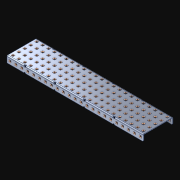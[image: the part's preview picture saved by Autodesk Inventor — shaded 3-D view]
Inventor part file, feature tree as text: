
AUTODESK INVENTOR PART (.ipt)
format: ipt  version: 2021 (Build 250183000, 183)  size: 2,080,256 bytes
history: native  units: in
note: dims shown in document units (in); Inventor stores cm internally (conversion verified against a paired STEP export)
features: extrude x162, other x162, sketch x4, pattern_linear x3
ambient origin geometry x8: Origin, YZ Plane, XZ Plane, XY Plane, X Axis, Y Axis, Z Axis, Center Point
bodies: Solid1 (feature_tree)
feature tree (331):
  pattern_linear  "Rectangular Pattern1"  Spacing1=0.182in  [1 undecoded]
  pattern_linear  "Rectangular Pattern2"  Spacing1=0.046in  [1 undecoded]
  pattern_linear  "Rectangular Pattern3"  Spacing1=0.5in  [1 undecoded]
  extrude  "Extrusion1"  Depth=0.046in
  sketch  "Sketch1"  dims[d0=0.182in]
  other  "Srf1"
  sketch  "Sketch2"  dims[d1=0.046in d2=0.0in]
  other  "Srf2"
  sketch  "Sketch3"  dims[d3=0.182in]
  other  "Srf3"
  other  "Srf4"
  other  "Srf5"
  other  "Srf6"
  other  "Srf7"
  other  "Srf8"
  other  "Srf9"
  other  "Srf10"
  other  "Srf11"
  other  "Srf12"
  other  "Srf13"
  other  "Srf14"
  other  "Srf15"
  other  "Srf16"
  other  "Srf17"
  other  "Srf18"
  other  "Srf19"
  other  "Srf20"
  other  "Srf21"
  other  "Srf22"
  other  "Srf23"
  other  "Srf24"
  other  "Srf25"
  other  "Srf38"
  other  "Srf39"
  other  "Srf40"
  other  "Srf41"
  other  "Srf42"
  other  "Srf43"
  other  "Srf44"
  other  "Srf45"
  other  "Srf46"
  other  "Srf47"
  other  "Srf48"
  other  "Srf49"
  other  "Srf50"
  other  "Srf51"
  other  "Srf52"
  other  "Srf53"
  other  "Srf54"
  other  "Srf55"
  other  "Srf56"
  other  "Srf57"
  other  "Srf58"
  other  "Srf59"
  other  "Srf72"
  other  "Srf73"
  other  "Srf74"
  other  "Srf75"
  other  "Srf76"
  other  "Srf77"
  other  "Srf78"
  other  "Srf79"
  other  "Srf80"
  other  "Srf81"
  other  "Srf82"
  other  "Srf83"
  other  "Srf84"
  other  "Srf85"
  other  "Srf86"
  other  "Srf87"
  other  "Srf88"
  other  "Srf89"
  other  "Srf90"
  other  "Srf91"
  other  "Srf92"
  other  "Srf93"
  other  "Srf94"
  other  "Srf107"
  other  "Srf108"
  other  "Srf109"
  other  "Srf110"
  other  "Srf111"
  other  "Srf112"
  other  "Srf113"
  other  "Srf114"
  other  "Srf115"
  other  "Srf116"
  other  "Srf117"
  other  "Srf118"
  other  "Srf119"
  other  "Srf120"
  other  "Srf121"
  other  "Srf122"
  other  "Srf123"
  other  "Srf124"
  other  "Srf125"
  other  "Srf126"
  other  "Srf127"
  other  "Srf128"
  other  "Srf129"
  other  "Srf142"
  other  "Srf143"
  other  "Srf144"
  other  "Srf145"
  other  "Srf146"
  other  "Srf147"
  other  "Srf148"
  other  "Srf149"
  other  "Srf150"
  other  "Srf151"
  other  "Srf152"
  other  "Srf153"
  other  "Srf154"
  other  "Srf155"
  other  "Srf156"
  other  "Srf157"
  other  "Srf158"
  other  "Srf159"
  other  "Srf160"
  other  "Srf161"
  other  "Srf162"
  other  "Srf163"
  other  "Srf164"
  other  "Srf177"
  other  "Srf178"
  other  "Srf179"
  other  "Srf180"
  other  "Srf181"
  other  "Srf182"
  other  "Srf183"
  other  "Srf184"
  other  "Srf185"
  other  "Srf186"
  other  "Srf187"
  other  "Srf188"
  other  "Srf189"
  other  "Srf190"
  other  "Srf191"
  other  "Srf192"
  other  "Srf193"
  other  "Srf194"
  other  "Srf195"
  other  "Srf196"
  other  "Srf197"
  other  "Srf198"
  other  "Srf199"
  other  "Srf212"
  other  "Srf213"
  other  "Srf214"
  other  "Srf215"
  other  "Srf216"
  other  "Srf217"
  other  "Srf218"
  other  "Srf219"
  other  "Srf220"
  other  "Srf221"
  other  "Srf222"
  other  "Srf223"
  other  "Srf224"
  other  "Srf225"
  other  "Srf226"
  other  "Srf227"
  other  "Srf228"
  other  "Srf229"
  other  "Srf230"
  other  "Srf231"
  other  "Srf232"
  other  "Srf233"
  sketch  "Sketch4"  dims[d4=0.046in d5=0.0in d6=0.182in d7=0.046in d8=0.0in d11=0.5in d12=9.0551in d14=0.5in d15=1.9685in d17=0.5in d18=9.0551in d20=0.5in d21=6.0in d22=0.0in]
  parser-record x1  (decoder bookkeeping rows leaked as tree rows — omitted from the tree; the rows remain in map.json)
  extrude  "ExtrusionSrf1"  Depth=0.046in
  extrude  "ExtrusionSrf2"  Depth=0.046in
  extrude  "ExtrusionSrf3"  Depth=0.046in
  extrude  "ExtrusionSrf4"  Depth=0.046in
  extrude  "ExtrusionSrf5"  Depth=0.046in
  extrude  "ExtrusionSrf6"  TaperAngle=0.0deg  [1 undecoded]
  extrude  "ExtrusionSrf7"  [1 undecoded]
  extrude  "ExtrusionSrf8"  [1 undecoded]
  extrude  "ExtrusionSrf9"  [1 undecoded]
  extrude  "ExtrusionSrf10"  [1 undecoded]
  extrude  "ExtrusionSrf11"  [1 undecoded]
  extrude  "ExtrusionSrf12"  [1 undecoded]
  extrude  "ExtrusionSrf13"  [1 undecoded]
  extrude  "ExtrusionSrf14"  [1 undecoded]
  extrude  "ExtrusionSrf15"  [1 undecoded]
  extrude  "ExtrusionSrf16"  [1 undecoded]
  extrude  "ExtrusionSrf17"  [1 undecoded]
  extrude  "ExtrusionSrf18"  [1 undecoded]
  extrude  "ExtrusionSrf19"  [1 undecoded]
  extrude  "ExtrusionSrf20"  [1 undecoded]
  extrude  "ExtrusionSrf21"  [1 undecoded]
  extrude  "ExtrusionSrf22"  [1 undecoded]
  extrude  "ExtrusionSrf23"  [1 undecoded]
  extrude  "ExtrusionSrf24"  [1 undecoded]
  extrude  "ExtrusionSrf25"  [1 undecoded]
  extrude  "ExtrusionSrf38"  [1 undecoded]
  extrude  "ExtrusionSrf39"  [1 undecoded]
  extrude  "ExtrusionSrf40"  [1 undecoded]
  extrude  "ExtrusionSrf41"  [1 undecoded]
  extrude  "ExtrusionSrf42"  [1 undecoded]
  extrude  "ExtrusionSrf43"  [1 undecoded]
  extrude  "ExtrusionSrf44"  [1 undecoded]
  extrude  "ExtrusionSrf45"  [1 undecoded]
  extrude  "ExtrusionSrf46"  [1 undecoded]
  extrude  "ExtrusionSrf47"  [1 undecoded]
  extrude  "ExtrusionSrf48"  [1 undecoded]
  extrude  "ExtrusionSrf49"  [1 undecoded]
  extrude  "ExtrusionSrf50"  [1 undecoded]
  extrude  "ExtrusionSrf51"  [1 undecoded]
  extrude  "ExtrusionSrf52"  [1 undecoded]
  extrude  "ExtrusionSrf53"  [1 undecoded]
  extrude  "ExtrusionSrf54"  [1 undecoded]
  extrude  "ExtrusionSrf55"  [1 undecoded]
  extrude  "ExtrusionSrf56"  [1 undecoded]
  extrude  "ExtrusionSrf57"  [1 undecoded]
  extrude  "ExtrusionSrf58"  [1 undecoded]
  extrude  "ExtrusionSrf59"  [1 undecoded]
  extrude  "ExtrusionSrf72"  [1 undecoded]
  extrude  "ExtrusionSrf73"  [1 undecoded]
  extrude  "ExtrusionSrf74"  [1 undecoded]
  extrude  "ExtrusionSrf75"  [1 undecoded]
  extrude  "ExtrusionSrf76"  [1 undecoded]
  extrude  "ExtrusionSrf77"  [1 undecoded]
  extrude  "ExtrusionSrf78"  [1 undecoded]
  extrude  "ExtrusionSrf79"  [1 undecoded]
  extrude  "ExtrusionSrf80"  [1 undecoded]
  extrude  "ExtrusionSrf81"  [1 undecoded]
  extrude  "ExtrusionSrf82"  [1 undecoded]
  extrude  "ExtrusionSrf83"  [1 undecoded]
  extrude  "ExtrusionSrf84"  [1 undecoded]
  extrude  "ExtrusionSrf85"  [1 undecoded]
  extrude  "ExtrusionSrf86"  [1 undecoded]
  extrude  "ExtrusionSrf87"  [1 undecoded]
  extrude  "ExtrusionSrf88"  [1 undecoded]
  extrude  "ExtrusionSrf89"  [1 undecoded]
  extrude  "ExtrusionSrf90"  [1 undecoded]
  extrude  "ExtrusionSrf91"  [1 undecoded]
  extrude  "ExtrusionSrf92"  [1 undecoded]
  extrude  "ExtrusionSrf93"  [1 undecoded]
  extrude  "ExtrusionSrf94"  [1 undecoded]
  extrude  "ExtrusionSrf107"  [1 undecoded]
  extrude  "ExtrusionSrf108"  [1 undecoded]
  extrude  "ExtrusionSrf109"  [1 undecoded]
  extrude  "ExtrusionSrf110"  [1 undecoded]
  extrude  "ExtrusionSrf111"  [1 undecoded]
  extrude  "ExtrusionSrf112"  [1 undecoded]
  extrude  "ExtrusionSrf113"  [1 undecoded]
  extrude  "ExtrusionSrf114"  [1 undecoded]
  extrude  "ExtrusionSrf115"  [1 undecoded]
  extrude  "ExtrusionSrf116"  [1 undecoded]
  extrude  "ExtrusionSrf117"  [1 undecoded]
  extrude  "ExtrusionSrf118"  [1 undecoded]
  extrude  "ExtrusionSrf119"  [1 undecoded]
  extrude  "ExtrusionSrf120"  [1 undecoded]
  extrude  "ExtrusionSrf121"  [1 undecoded]
  extrude  "ExtrusionSrf122"  [1 undecoded]
  extrude  "ExtrusionSrf123"  [1 undecoded]
  extrude  "ExtrusionSrf124"  [1 undecoded]
  extrude  "ExtrusionSrf125"  [1 undecoded]
  extrude  "ExtrusionSrf126"  [1 undecoded]
  extrude  "ExtrusionSrf127"  [1 undecoded]
  extrude  "ExtrusionSrf128"  [1 undecoded]
  extrude  "ExtrusionSrf129"  [1 undecoded]
  extrude  "ExtrusionSrf142"  [1 undecoded]
  extrude  "ExtrusionSrf143"  [1 undecoded]
  extrude  "ExtrusionSrf144"  [1 undecoded]
  extrude  "ExtrusionSrf145"  [1 undecoded]
  extrude  "ExtrusionSrf146"  [1 undecoded]
  extrude  "ExtrusionSrf147"  [1 undecoded]
  extrude  "ExtrusionSrf148"  [1 undecoded]
  extrude  "ExtrusionSrf149"  [1 undecoded]
  extrude  "ExtrusionSrf150"  [1 undecoded]
  extrude  "ExtrusionSrf151"  [1 undecoded]
  extrude  "ExtrusionSrf152"  [1 undecoded]
  extrude  "ExtrusionSrf153"  [1 undecoded]
  extrude  "ExtrusionSrf154"  [1 undecoded]
  extrude  "ExtrusionSrf155"  [1 undecoded]
  extrude  "ExtrusionSrf156"  [1 undecoded]
  extrude  "ExtrusionSrf157"  [1 undecoded]
  extrude  "ExtrusionSrf158"  [1 undecoded]
  extrude  "ExtrusionSrf159"  [1 undecoded]
  extrude  "ExtrusionSrf160"  [1 undecoded]
  extrude  "ExtrusionSrf161"  [1 undecoded]
  extrude  "ExtrusionSrf162"  [1 undecoded]
  extrude  "ExtrusionSrf163"  [1 undecoded]
  extrude  "ExtrusionSrf164"  [1 undecoded]
  extrude  "ExtrusionSrf177"  [1 undecoded]
  extrude  "ExtrusionSrf178"  [1 undecoded]
  extrude  "ExtrusionSrf179"  [1 undecoded]
  extrude  "ExtrusionSrf180"  [1 undecoded]
  extrude  "ExtrusionSrf181"  [1 undecoded]
  extrude  "ExtrusionSrf182"  [1 undecoded]
  extrude  "ExtrusionSrf183"  [1 undecoded]
  extrude  "ExtrusionSrf184"  [1 undecoded]
  extrude  "ExtrusionSrf185"  [1 undecoded]
  extrude  "ExtrusionSrf186"  [1 undecoded]
  extrude  "ExtrusionSrf187"  [1 undecoded]
  extrude  "ExtrusionSrf188"  [1 undecoded]
  extrude  "ExtrusionSrf189"  [1 undecoded]
  extrude  "ExtrusionSrf190"  [1 undecoded]
  extrude  "ExtrusionSrf191"  [1 undecoded]
  extrude  "ExtrusionSrf192"  [1 undecoded]
  extrude  "ExtrusionSrf193"  [1 undecoded]
  extrude  "ExtrusionSrf194"  [1 undecoded]
  extrude  "ExtrusionSrf195"  [1 undecoded]
  extrude  "ExtrusionSrf196"  [1 undecoded]
  extrude  "ExtrusionSrf197"  [1 undecoded]
  extrude  "ExtrusionSrf198"  [1 undecoded]
  extrude  "ExtrusionSrf199"  [1 undecoded]
  extrude  "ExtrusionSrf212"  [1 undecoded]
  extrude  "ExtrusionSrf213"  [1 undecoded]
  extrude  "ExtrusionSrf214"  [1 undecoded]
  extrude  "ExtrusionSrf215"  [1 undecoded]
  extrude  "ExtrusionSrf216"  [1 undecoded]
  extrude  "ExtrusionSrf217"  [1 undecoded]
  extrude  "ExtrusionSrf218"  [1 undecoded]
  extrude  "ExtrusionSrf219"  [1 undecoded]
  extrude  "ExtrusionSrf220"  [1 undecoded]
  extrude  "ExtrusionSrf221"  [1 undecoded]
  extrude  "ExtrusionSrf222"  [1 undecoded]
  extrude  "ExtrusionSrf223"  [1 undecoded]
  extrude  "ExtrusionSrf224"  [1 undecoded]
  extrude  "ExtrusionSrf225"  [1 undecoded]
  extrude  "ExtrusionSrf226"  [1 undecoded]
  extrude  "ExtrusionSrf227"  [1 undecoded]
  extrude  "ExtrusionSrf228"  [1 undecoded]
  extrude  "ExtrusionSrf229"  [1 undecoded]
  extrude  "ExtrusionSrf230"  [1 undecoded]
  extrude  "ExtrusionSrf231"  [1 undecoded]
  extrude  "ExtrusionSrf232"  [1 undecoded]
  extrude  "ExtrusionSrf233"  [1 undecoded]
note: 159 required parameter values undecoded (feature->parameter linkage not recoverable at this tier; creation-order binding heuristic only, values carry confidence <= 0.55)
